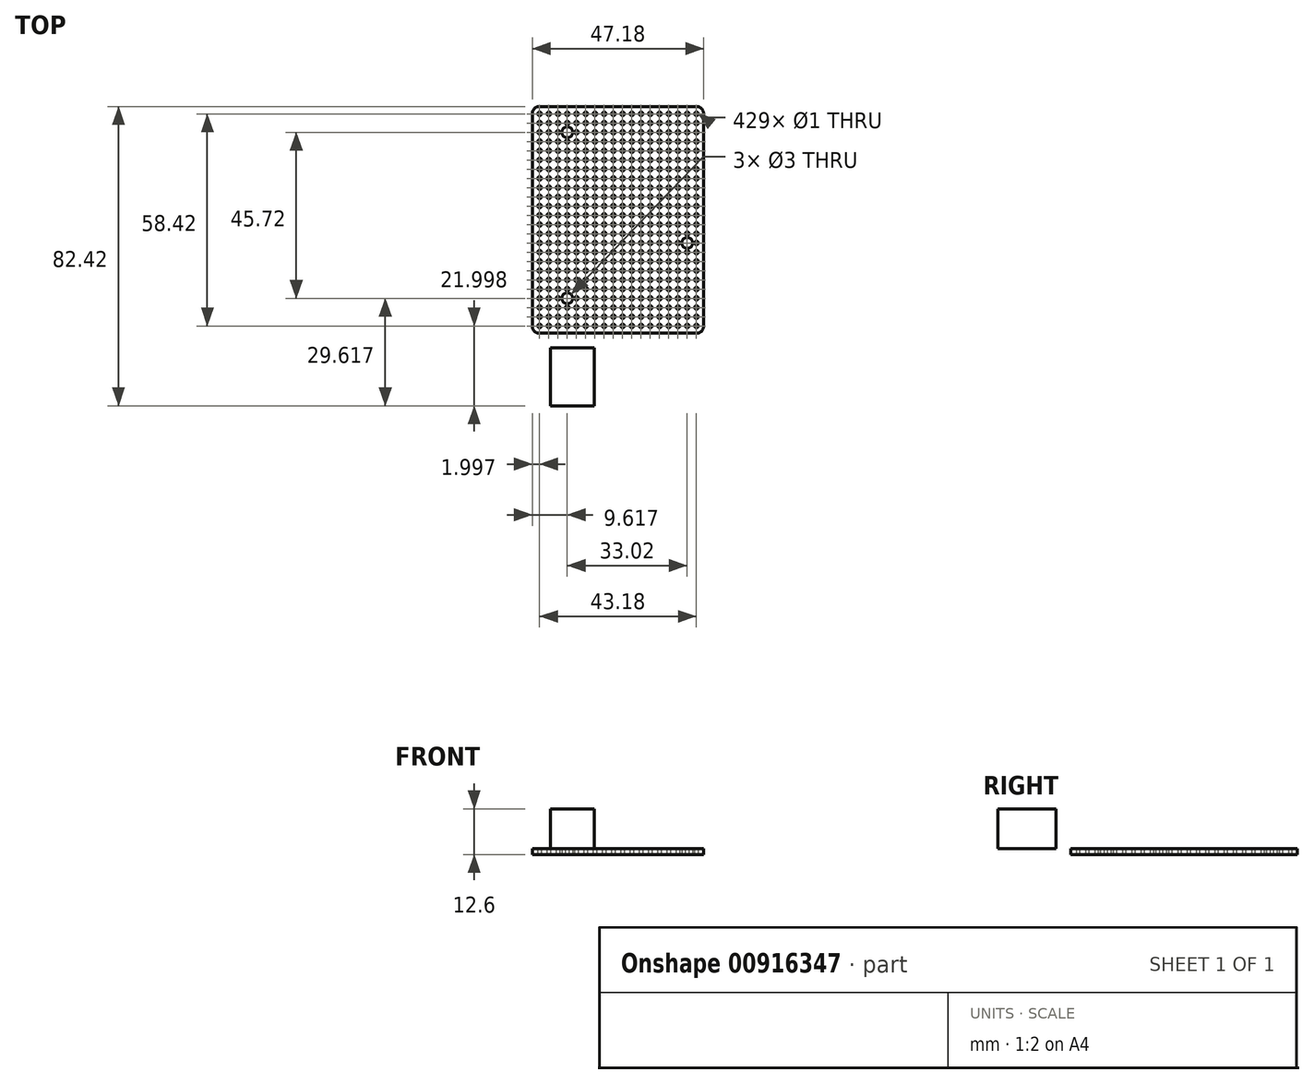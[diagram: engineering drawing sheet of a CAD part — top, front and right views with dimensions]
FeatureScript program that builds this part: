
annotation { "Feature Type Name" : "Feature", "Feature Type Description" : "" }
export const myFeature = defineFeature(function(context is Context, id is Id, definition is map)
    precondition{}
    {
        {
            var Q0;
            Q0=qCreatedBy(makeId("Top.planeOp"),FACE);
            var sketch = newSketch(context, id + "F0", { "sketchPlane" : qUnion([Q0])});
            skLineSegment(sketch, "E0.bottom", {"start": v(-24.1, 49.25) * mm, "end": v(23.09, 49.25) * mm});
            skLineSegment(sketch, "E0.top", {"start": v(-24.1, -13.17) * mm, "end": v(23.09, -13.17) * mm});
            skLineSegment(sketch, "E0.left", {"start": v(-24.1, 49.25) * mm, "end": v(-24.1, -13.17) * mm});
            skLineSegment(sketch, "E0.right", {"start": v(23.09, 49.25) * mm, "end": v(23.09, -13.17) * mm});
            skCircle(sketch, "E1", {"center": v(-22.1, 47.25) * mm, "radius": 0.5 * mm});
            skCircle(sketch, "E2.0.1.0", {"center": v(-22.1, 44.7) * mm, "radius": 0.5 * mm});
            skCircle(sketch, "E2.0.2.0", {"center": v(-22.1, 42.17) * mm, "radius": 0.5 * mm});
            skCircle(sketch, "E2.0.3.0", {"center": v(-22.1, 39.63) * mm, "radius": 0.5 * mm});
            skCircle(sketch, "E2.0.4.0", {"center": v(-22.1, 37.09) * mm, "radius": 0.5 * mm});
            skCircle(sketch, "E2.0.5.0", {"center": v(-22.1, 34.55) * mm, "radius": 0.5 * mm});
            skCircle(sketch, "E2.0.6.0", {"center": v(-22.1, 32) * mm, "radius": 0.5 * mm});
            skCircle(sketch, "E2.0.7.0", {"center": v(-22.1, 29.47) * mm, "radius": 0.5 * mm});
            skCircle(sketch, "E2.0.8.0", {"center": v(-22.1, 26.93) * mm, "radius": 0.5 * mm});
            skCircle(sketch, "E2.0.9.0", {"center": v(-22.1, 24.39) * mm, "radius": 0.5 * mm});
            skCircle(sketch, "E2.0.10.0", {"center": v(-22.1, 21.85) * mm, "radius": 0.5 * mm});
            skCircle(sketch, "E2.0.11.0", {"center": v(-22.1, 19.3) * mm, "radius": 0.5 * mm});
            skCircle(sketch, "E2.0.12.0", {"center": v(-22.1, 16.77) * mm, "radius": 0.5 * mm});
            skCircle(sketch, "E2.0.13.0", {"center": v(-22.1, 14.23) * mm, "radius": 0.5 * mm});
            skCircle(sketch, "E2.0.14.0", {"center": v(-22.1, 11.69) * mm, "radius": 0.5 * mm});
            skCircle(sketch, "E2.0.15.0", {"center": v(-22.1, 9.15) * mm, "radius": 0.5 * mm});
            skCircle(sketch, "E2.0.16.0", {"center": v(-22.1, 6.6) * mm, "radius": 0.5 * mm});
            skCircle(sketch, "E2.0.17.0", {"center": v(-22.1, 4.07) * mm, "radius": 0.5 * mm});
            skCircle(sketch, "E2.0.18.0", {"center": v(-22.1, 1.53) * mm, "radius": 0.5 * mm});
            skCircle(sketch, "E2.0.19.0", {"center": v(-22.1, -1.01) * mm, "radius": 0.5 * mm});
            skCircle(sketch, "E2.0.20.0", {"center": v(-22.1, -3.55) * mm, "radius": 0.5 * mm});
            skCircle(sketch, "E2.0.21.0", {"center": v(-22.1, -6.1) * mm, "radius": 0.5 * mm});
            skCircle(sketch, "E2.0.22.0", {"center": v(-22.1, -8.63) * mm, "radius": 0.5 * mm});
            skCircle(sketch, "E2.0.23.0", {"center": v(-22.1, -11.17) * mm, "radius": 0.5 * mm});
            skCircle(sketch, "E2.1.0.0", {"center": v(-19.55, 47.25) * mm, "radius": 0.5 * mm});
            skCircle(sketch, "E2.1.1.0", {"center": v(-19.55, 44.7) * mm, "radius": 0.5 * mm});
            skCircle(sketch, "E2.1.2.0", {"center": v(-19.55, 42.17) * mm, "radius": 0.5 * mm});
            skCircle(sketch, "E2.1.3.0", {"center": v(-19.55, 39.63) * mm, "radius": 0.5 * mm});
            skCircle(sketch, "E2.1.4.0", {"center": v(-19.55, 37.09) * mm, "radius": 0.5 * mm});
            skCircle(sketch, "E2.1.5.0", {"center": v(-19.55, 34.55) * mm, "radius": 0.5 * mm});
            skCircle(sketch, "E2.1.6.0", {"center": v(-19.55, 32) * mm, "radius": 0.5 * mm});
            skCircle(sketch, "E2.1.7.0", {"center": v(-19.55, 29.47) * mm, "radius": 0.5 * mm});
            skCircle(sketch, "E2.1.8.0", {"center": v(-19.55, 26.93) * mm, "radius": 0.5 * mm});
            skCircle(sketch, "E2.1.9.0", {"center": v(-19.55, 24.39) * mm, "radius": 0.5 * mm});
            skCircle(sketch, "E2.1.10.0", {"center": v(-19.55, 21.85) * mm, "radius": 0.5 * mm});
            skCircle(sketch, "E2.1.11.0", {"center": v(-19.55, 19.3) * mm, "radius": 0.5 * mm});
            skCircle(sketch, "E2.1.12.0", {"center": v(-19.55, 16.77) * mm, "radius": 0.5 * mm});
            skCircle(sketch, "E2.1.13.0", {"center": v(-19.55, 14.23) * mm, "radius": 0.5 * mm});
            skCircle(sketch, "E2.1.14.0", {"center": v(-19.55, 11.69) * mm, "radius": 0.5 * mm});
            skCircle(sketch, "E2.1.15.0", {"center": v(-19.55, 9.15) * mm, "radius": 0.5 * mm});
            skCircle(sketch, "E2.1.16.0", {"center": v(-19.55, 6.6) * mm, "radius": 0.5 * mm});
            skCircle(sketch, "E2.1.17.0", {"center": v(-19.55, 4.07) * mm, "radius": 0.5 * mm});
            skCircle(sketch, "E2.1.18.0", {"center": v(-19.55, 1.53) * mm, "radius": 0.5 * mm});
            skCircle(sketch, "E2.1.19.0", {"center": v(-19.55, -1.01) * mm, "radius": 0.5 * mm});
            skCircle(sketch, "E2.1.20.0", {"center": v(-19.55, -3.55) * mm, "radius": 0.5 * mm});
            skCircle(sketch, "E2.1.21.0", {"center": v(-19.55, -6.1) * mm, "radius": 0.5 * mm});
            skCircle(sketch, "E2.1.22.0", {"center": v(-19.55, -8.63) * mm, "radius": 0.5 * mm});
            skCircle(sketch, "E2.1.23.0", {"center": v(-19.55, -11.17) * mm, "radius": 0.5 * mm});
            skCircle(sketch, "E2.2.0.0", {"center": v(-17.01, 47.25) * mm, "radius": 0.5 * mm});
            skCircle(sketch, "E2.2.1.0", {"center": v(-17.01, 44.7) * mm, "radius": 0.5 * mm});
            skCircle(sketch, "E2.2.2.0", {"center": v(-17.01, 42.17) * mm, "radius": 0.5 * mm});
            skCircle(sketch, "E2.2.3.0", {"center": v(-17.01, 39.63) * mm, "radius": 0.5 * mm});
            skCircle(sketch, "E2.2.4.0", {"center": v(-17.01, 37.09) * mm, "radius": 0.5 * mm});
            skCircle(sketch, "E2.2.5.0", {"center": v(-17.01, 34.55) * mm, "radius": 0.5 * mm});
            skCircle(sketch, "E2.2.6.0", {"center": v(-17.01, 32) * mm, "radius": 0.5 * mm});
            skCircle(sketch, "E2.2.7.0", {"center": v(-17.01, 29.47) * mm, "radius": 0.5 * mm});
            skCircle(sketch, "E2.2.8.0", {"center": v(-17.01, 26.93) * mm, "radius": 0.5 * mm});
            skCircle(sketch, "E2.2.9.0", {"center": v(-17.01, 24.39) * mm, "radius": 0.5 * mm});
            skCircle(sketch, "E2.2.10.0", {"center": v(-17.01, 21.85) * mm, "radius": 0.5 * mm});
            skCircle(sketch, "E2.2.11.0", {"center": v(-17.01, 19.3) * mm, "radius": 0.5 * mm});
            skCircle(sketch, "E2.2.12.0", {"center": v(-17.01, 16.77) * mm, "radius": 0.5 * mm});
            skCircle(sketch, "E2.2.13.0", {"center": v(-17.01, 14.23) * mm, "radius": 0.5 * mm});
            skCircle(sketch, "E2.2.14.0", {"center": v(-17.01, 11.69) * mm, "radius": 0.5 * mm});
            skCircle(sketch, "E2.2.15.0", {"center": v(-17.01, 9.15) * mm, "radius": 0.5 * mm});
            skCircle(sketch, "E2.2.16.0", {"center": v(-17.01, 6.6) * mm, "radius": 0.5 * mm});
            skCircle(sketch, "E2.2.17.0", {"center": v(-17.01, 4.07) * mm, "radius": 0.5 * mm});
            skCircle(sketch, "E2.2.18.0", {"center": v(-17.01, 1.53) * mm, "radius": 0.5 * mm});
            skCircle(sketch, "E2.2.19.0", {"center": v(-17.01, -1.01) * mm, "radius": 0.5 * mm});
            skCircle(sketch, "E2.2.20.0", {"center": v(-17.01, -3.55) * mm, "radius": 0.5 * mm});
            skCircle(sketch, "E2.2.21.0", {"center": v(-17.01, -6.1) * mm, "radius": 0.5 * mm});
            skCircle(sketch, "E2.2.22.0", {"center": v(-17.01, -8.63) * mm, "radius": 0.5 * mm});
            skCircle(sketch, "E2.2.23.0", {"center": v(-17.01, -11.17) * mm, "radius": 0.5 * mm});
            skCircle(sketch, "E2.3.0.0", {"center": v(-14.47, 47.25) * mm, "radius": 0.5 * mm});
            skCircle(sketch, "E2.3.1.0", {"center": v(-14.47, 44.7) * mm, "radius": 0.5 * mm});
            skCircle(sketch, "E2.3.2.0", {"center": v(-14.47, 42.17) * mm, "radius": 0.5 * mm});
            skCircle(sketch, "E2.3.3.0", {"center": v(-14.47, 39.63) * mm, "radius": 0.5 * mm});
            skCircle(sketch, "E2.3.4.0", {"center": v(-14.47, 37.09) * mm, "radius": 0.5 * mm});
            skCircle(sketch, "E2.3.5.0", {"center": v(-14.47, 34.55) * mm, "radius": 0.5 * mm});
            skCircle(sketch, "E2.3.6.0", {"center": v(-14.47, 32) * mm, "radius": 0.5 * mm});
            skCircle(sketch, "E2.3.7.0", {"center": v(-14.47, 29.47) * mm, "radius": 0.5 * mm});
            skCircle(sketch, "E2.3.8.0", {"center": v(-14.47, 26.93) * mm, "radius": 0.5 * mm});
            skCircle(sketch, "E2.3.9.0", {"center": v(-14.47, 24.39) * mm, "radius": 0.5 * mm});
            skCircle(sketch, "E2.3.10.0", {"center": v(-14.47, 21.85) * mm, "radius": 0.5 * mm});
            skCircle(sketch, "E2.3.11.0", {"center": v(-14.47, 19.3) * mm, "radius": 0.5 * mm});
            skCircle(sketch, "E2.3.12.0", {"center": v(-14.47, 16.77) * mm, "radius": 0.5 * mm});
            skCircle(sketch, "E2.3.13.0", {"center": v(-14.47, 14.23) * mm, "radius": 0.5 * mm});
            skCircle(sketch, "E2.3.14.0", {"center": v(-14.47, 11.69) * mm, "radius": 0.5 * mm});
            skCircle(sketch, "E2.3.15.0", {"center": v(-14.47, 9.15) * mm, "radius": 0.5 * mm});
            skCircle(sketch, "E2.3.16.0", {"center": v(-14.47, 6.6) * mm, "radius": 0.5 * mm});
            skCircle(sketch, "E2.3.17.0", {"center": v(-14.47, 4.07) * mm, "radius": 0.5 * mm});
            skCircle(sketch, "E2.3.18.0", {"center": v(-14.47, 1.53) * mm, "radius": 0.5 * mm});
            skCircle(sketch, "E2.3.19.0", {"center": v(-14.47, -1.01) * mm, "radius": 0.5 * mm});
            skCircle(sketch, "E2.3.20.0", {"center": v(-14.47, -3.55) * mm, "radius": 0.5 * mm});
            skCircle(sketch, "E2.3.21.0", {"center": v(-14.47, -6.1) * mm, "radius": 0.5 * mm});
            skCircle(sketch, "E2.3.22.0", {"center": v(-14.47, -8.63) * mm, "radius": 0.5 * mm});
            skCircle(sketch, "E2.3.23.0", {"center": v(-14.47, -11.17) * mm, "radius": 0.5 * mm});
            skCircle(sketch, "E2.4.0.0", {"center": v(-11.93, 47.25) * mm, "radius": 0.5 * mm});
            skCircle(sketch, "E2.4.1.0", {"center": v(-11.93, 44.7) * mm, "radius": 0.5 * mm});
            skCircle(sketch, "E2.4.2.0", {"center": v(-11.93, 42.17) * mm, "radius": 0.5 * mm});
            skCircle(sketch, "E2.4.3.0", {"center": v(-11.93, 39.63) * mm, "radius": 0.5 * mm});
            skCircle(sketch, "E2.4.4.0", {"center": v(-11.93, 37.09) * mm, "radius": 0.5 * mm});
            skCircle(sketch, "E2.4.5.0", {"center": v(-11.93, 34.55) * mm, "radius": 0.5 * mm});
            skCircle(sketch, "E2.4.6.0", {"center": v(-11.93, 32) * mm, "radius": 0.5 * mm});
            skCircle(sketch, "E2.4.7.0", {"center": v(-11.93, 29.47) * mm, "radius": 0.5 * mm});
            skCircle(sketch, "E2.4.8.0", {"center": v(-11.93, 26.93) * mm, "radius": 0.5 * mm});
            skCircle(sketch, "E2.4.9.0", {"center": v(-11.93, 24.39) * mm, "radius": 0.5 * mm});
            skCircle(sketch, "E2.4.10.0", {"center": v(-11.93, 21.85) * mm, "radius": 0.5 * mm});
            skCircle(sketch, "E2.4.11.0", {"center": v(-11.93, 19.3) * mm, "radius": 0.5 * mm});
            skCircle(sketch, "E2.4.12.0", {"center": v(-11.93, 16.77) * mm, "radius": 0.5 * mm});
            skCircle(sketch, "E2.4.13.0", {"center": v(-11.93, 14.23) * mm, "radius": 0.5 * mm});
            skCircle(sketch, "E2.4.14.0", {"center": v(-11.93, 11.69) * mm, "radius": 0.5 * mm});
            skCircle(sketch, "E2.4.15.0", {"center": v(-11.93, 9.15) * mm, "radius": 0.5 * mm});
            skCircle(sketch, "E2.4.16.0", {"center": v(-11.93, 6.6) * mm, "radius": 0.5 * mm});
            skCircle(sketch, "E2.4.17.0", {"center": v(-11.93, 4.07) * mm, "radius": 0.5 * mm});
            skCircle(sketch, "E2.4.18.0", {"center": v(-11.93, 1.53) * mm, "radius": 0.5 * mm});
            skCircle(sketch, "E2.4.19.0", {"center": v(-11.93, -1.01) * mm, "radius": 0.5 * mm});
            skCircle(sketch, "E2.4.20.0", {"center": v(-11.93, -3.55) * mm, "radius": 0.5 * mm});
            skCircle(sketch, "E2.4.21.0", {"center": v(-11.93, -6.1) * mm, "radius": 0.5 * mm});
            skCircle(sketch, "E2.4.22.0", {"center": v(-11.93, -8.63) * mm, "radius": 0.5 * mm});
            skCircle(sketch, "E2.4.23.0", {"center": v(-11.93, -11.17) * mm, "radius": 0.5 * mm});
            skCircle(sketch, "E2.5.0.0", {"center": v(-9.4, 47.25) * mm, "radius": 0.5 * mm});
            skCircle(sketch, "E2.5.1.0", {"center": v(-9.4, 44.7) * mm, "radius": 0.5 * mm});
            skCircle(sketch, "E2.5.2.0", {"center": v(-9.4, 42.17) * mm, "radius": 0.5 * mm});
            skCircle(sketch, "E2.5.3.0", {"center": v(-9.4, 39.63) * mm, "radius": 0.5 * mm});
            skCircle(sketch, "E2.5.4.0", {"center": v(-9.4, 37.09) * mm, "radius": 0.5 * mm});
            skCircle(sketch, "E2.5.5.0", {"center": v(-9.4, 34.55) * mm, "radius": 0.5 * mm});
            skCircle(sketch, "E2.5.6.0", {"center": v(-9.4, 32) * mm, "radius": 0.5 * mm});
            skCircle(sketch, "E2.5.7.0", {"center": v(-9.4, 29.47) * mm, "radius": 0.5 * mm});
            skCircle(sketch, "E2.5.8.0", {"center": v(-9.4, 26.93) * mm, "radius": 0.5 * mm});
            skCircle(sketch, "E2.5.9.0", {"center": v(-9.4, 24.39) * mm, "radius": 0.5 * mm});
            skCircle(sketch, "E2.5.10.0", {"center": v(-9.4, 21.85) * mm, "radius": 0.5 * mm});
            skCircle(sketch, "E2.5.11.0", {"center": v(-9.4, 19.3) * mm, "radius": 0.5 * mm});
            skCircle(sketch, "E2.5.12.0", {"center": v(-9.4, 16.77) * mm, "radius": 0.5 * mm});
            skCircle(sketch, "E2.5.13.0", {"center": v(-9.4, 14.23) * mm, "radius": 0.5 * mm});
            skCircle(sketch, "E2.5.14.0", {"center": v(-9.4, 11.69) * mm, "radius": 0.5 * mm});
            skCircle(sketch, "E2.5.15.0", {"center": v(-9.4, 9.15) * mm, "radius": 0.5 * mm});
            skCircle(sketch, "E2.5.16.0", {"center": v(-9.4, 6.6) * mm, "radius": 0.5 * mm});
            skCircle(sketch, "E2.5.17.0", {"center": v(-9.4, 4.07) * mm, "radius": 0.5 * mm});
            skCircle(sketch, "E2.5.18.0", {"center": v(-9.4, 1.53) * mm, "radius": 0.5 * mm});
            skCircle(sketch, "E2.5.19.0", {"center": v(-9.4, -1.01) * mm, "radius": 0.5 * mm});
            skCircle(sketch, "E2.5.20.0", {"center": v(-9.4, -3.55) * mm, "radius": 0.5 * mm});
            skCircle(sketch, "E2.5.21.0", {"center": v(-9.4, -6.1) * mm, "radius": 0.5 * mm});
            skCircle(sketch, "E2.5.22.0", {"center": v(-9.4, -8.63) * mm, "radius": 0.5 * mm});
            skCircle(sketch, "E2.5.23.0", {"center": v(-9.4, -11.17) * mm, "radius": 0.5 * mm});
            skCircle(sketch, "E2.6.0.0", {"center": v(-6.85, 47.25) * mm, "radius": 0.5 * mm});
            skCircle(sketch, "E2.6.1.0", {"center": v(-6.85, 44.7) * mm, "radius": 0.5 * mm});
            skCircle(sketch, "E2.6.2.0", {"center": v(-6.85, 42.17) * mm, "radius": 0.5 * mm});
            skCircle(sketch, "E2.6.3.0", {"center": v(-6.85, 39.63) * mm, "radius": 0.5 * mm});
            skCircle(sketch, "E2.6.4.0", {"center": v(-6.85, 37.09) * mm, "radius": 0.5 * mm});
            skCircle(sketch, "E2.6.5.0", {"center": v(-6.85, 34.55) * mm, "radius": 0.5 * mm});
            skCircle(sketch, "E2.6.6.0", {"center": v(-6.85, 32) * mm, "radius": 0.5 * mm});
            skCircle(sketch, "E2.6.7.0", {"center": v(-6.85, 29.47) * mm, "radius": 0.5 * mm});
            skCircle(sketch, "E2.6.8.0", {"center": v(-6.85, 26.93) * mm, "radius": 0.5 * mm});
            skCircle(sketch, "E2.6.9.0", {"center": v(-6.85, 24.39) * mm, "radius": 0.5 * mm});
            skCircle(sketch, "E2.6.10.0", {"center": v(-6.85, 21.85) * mm, "radius": 0.5 * mm});
            skCircle(sketch, "E2.6.11.0", {"center": v(-6.85, 19.3) * mm, "radius": 0.5 * mm});
            skCircle(sketch, "E2.6.12.0", {"center": v(-6.85, 16.77) * mm, "radius": 0.5 * mm});
            skCircle(sketch, "E2.6.13.0", {"center": v(-6.85, 14.23) * mm, "radius": 0.5 * mm});
            skCircle(sketch, "E2.6.14.0", {"center": v(-6.85, 11.69) * mm, "radius": 0.5 * mm});
            skCircle(sketch, "E2.6.15.0", {"center": v(-6.85, 9.15) * mm, "radius": 0.5 * mm});
            skCircle(sketch, "E2.6.16.0", {"center": v(-6.85, 6.6) * mm, "radius": 0.5 * mm});
            skCircle(sketch, "E2.6.17.0", {"center": v(-6.85, 4.07) * mm, "radius": 0.5 * mm});
            skCircle(sketch, "E2.6.18.0", {"center": v(-6.85, 1.53) * mm, "radius": 0.5 * mm});
            skCircle(sketch, "E2.6.19.0", {"center": v(-6.85, -1.01) * mm, "radius": 0.5 * mm});
            skCircle(sketch, "E2.6.20.0", {"center": v(-6.85, -3.55) * mm, "radius": 0.5 * mm});
            skCircle(sketch, "E2.6.21.0", {"center": v(-6.85, -6.1) * mm, "radius": 0.5 * mm});
            skCircle(sketch, "E2.6.22.0", {"center": v(-6.85, -8.63) * mm, "radius": 0.5 * mm});
            skCircle(sketch, "E2.6.23.0", {"center": v(-6.85, -11.17) * mm, "radius": 0.5 * mm});
            skCircle(sketch, "E2.7.0.0", {"center": v(-4.31, 47.25) * mm, "radius": 0.5 * mm});
            skCircle(sketch, "E2.7.1.0", {"center": v(-4.31, 44.7) * mm, "radius": 0.5 * mm});
            skCircle(sketch, "E2.7.2.0", {"center": v(-4.31, 42.17) * mm, "radius": 0.5 * mm});
            skCircle(sketch, "E2.7.3.0", {"center": v(-4.31, 39.63) * mm, "radius": 0.5 * mm});
            skCircle(sketch, "E2.7.4.0", {"center": v(-4.31, 37.09) * mm, "radius": 0.5 * mm});
            skCircle(sketch, "E2.7.5.0", {"center": v(-4.31, 34.55) * mm, "radius": 0.5 * mm});
            skCircle(sketch, "E2.7.6.0", {"center": v(-4.31, 32) * mm, "radius": 0.5 * mm});
            skCircle(sketch, "E2.7.7.0", {"center": v(-4.31, 29.47) * mm, "radius": 0.5 * mm});
            skCircle(sketch, "E2.7.8.0", {"center": v(-4.31, 26.93) * mm, "radius": 0.5 * mm});
            skCircle(sketch, "E2.7.9.0", {"center": v(-4.31, 24.39) * mm, "radius": 0.5 * mm});
            skCircle(sketch, "E2.7.10.0", {"center": v(-4.31, 21.85) * mm, "radius": 0.5 * mm});
            skCircle(sketch, "E2.7.11.0", {"center": v(-4.31, 19.3) * mm, "radius": 0.5 * mm});
            skCircle(sketch, "E2.7.12.0", {"center": v(-4.31, 16.77) * mm, "radius": 0.5 * mm});
            skCircle(sketch, "E2.7.13.0", {"center": v(-4.31, 14.23) * mm, "radius": 0.5 * mm});
            skCircle(sketch, "E2.7.14.0", {"center": v(-4.31, 11.69) * mm, "radius": 0.5 * mm});
            skCircle(sketch, "E2.7.15.0", {"center": v(-4.31, 9.15) * mm, "radius": 0.5 * mm});
            skCircle(sketch, "E2.7.16.0", {"center": v(-4.31, 6.6) * mm, "radius": 0.5 * mm});
            skCircle(sketch, "E2.7.17.0", {"center": v(-4.31, 4.07) * mm, "radius": 0.5 * mm});
            skCircle(sketch, "E2.7.18.0", {"center": v(-4.31, 1.53) * mm, "radius": 0.5 * mm});
            skCircle(sketch, "E2.7.19.0", {"center": v(-4.31, -1.01) * mm, "radius": 0.5 * mm});
            skCircle(sketch, "E2.7.20.0", {"center": v(-4.31, -3.55) * mm, "radius": 0.5 * mm});
            skCircle(sketch, "E2.7.21.0", {"center": v(-4.31, -6.1) * mm, "radius": 0.5 * mm});
            skCircle(sketch, "E2.7.22.0", {"center": v(-4.31, -8.63) * mm, "radius": 0.5 * mm});
            skCircle(sketch, "E2.7.23.0", {"center": v(-4.31, -11.17) * mm, "radius": 0.5 * mm});
            skCircle(sketch, "E2.8.0.0", {"center": v(-1.77, 47.25) * mm, "radius": 0.5 * mm});
            skCircle(sketch, "E2.8.1.0", {"center": v(-1.77, 44.7) * mm, "radius": 0.5 * mm});
            skCircle(sketch, "E2.8.2.0", {"center": v(-1.77, 42.17) * mm, "radius": 0.5 * mm});
            skCircle(sketch, "E2.8.3.0", {"center": v(-1.77, 39.63) * mm, "radius": 0.5 * mm});
            skCircle(sketch, "E2.8.4.0", {"center": v(-1.77, 37.09) * mm, "radius": 0.5 * mm});
            skCircle(sketch, "E2.8.5.0", {"center": v(-1.77, 34.55) * mm, "radius": 0.5 * mm});
            skCircle(sketch, "E2.8.6.0", {"center": v(-1.77, 32) * mm, "radius": 0.5 * mm});
            skCircle(sketch, "E2.8.7.0", {"center": v(-1.77, 29.47) * mm, "radius": 0.5 * mm});
            skCircle(sketch, "E2.8.8.0", {"center": v(-1.77, 26.93) * mm, "radius": 0.5 * mm});
            skCircle(sketch, "E2.8.9.0", {"center": v(-1.77, 24.39) * mm, "radius": 0.5 * mm});
            skCircle(sketch, "E2.8.10.0", {"center": v(-1.77, 21.85) * mm, "radius": 0.5 * mm});
            skCircle(sketch, "E2.8.11.0", {"center": v(-1.77, 19.3) * mm, "radius": 0.5 * mm});
            skCircle(sketch, "E2.8.12.0", {"center": v(-1.77, 16.77) * mm, "radius": 0.5 * mm});
            skCircle(sketch, "E2.8.13.0", {"center": v(-1.77, 14.23) * mm, "radius": 0.5 * mm});
            skCircle(sketch, "E2.8.14.0", {"center": v(-1.77, 11.69) * mm, "radius": 0.5 * mm});
            skCircle(sketch, "E2.8.15.0", {"center": v(-1.77, 9.15) * mm, "radius": 0.5 * mm});
            skCircle(sketch, "E2.8.16.0", {"center": v(-1.77, 6.6) * mm, "radius": 0.5 * mm});
            skCircle(sketch, "E2.8.17.0", {"center": v(-1.77, 4.07) * mm, "radius": 0.5 * mm});
            skCircle(sketch, "E2.8.18.0", {"center": v(-1.77, 1.53) * mm, "radius": 0.5 * mm});
            skCircle(sketch, "E2.8.19.0", {"center": v(-1.77, -1.01) * mm, "radius": 0.5 * mm});
            skCircle(sketch, "E2.8.20.0", {"center": v(-1.77, -3.55) * mm, "radius": 0.5 * mm});
            skCircle(sketch, "E2.8.21.0", {"center": v(-1.77, -6.1) * mm, "radius": 0.5 * mm});
            skCircle(sketch, "E2.8.22.0", {"center": v(-1.77, -8.63) * mm, "radius": 0.5 * mm});
            skCircle(sketch, "E2.8.23.0", {"center": v(-1.77, -11.17) * mm, "radius": 0.5 * mm});
            skCircle(sketch, "E2.9.0.0", {"center": v(0.77, 47.25) * mm, "radius": 0.5 * mm});
            skCircle(sketch, "E2.9.1.0", {"center": v(0.77, 44.7) * mm, "radius": 0.5 * mm});
            skCircle(sketch, "E2.9.2.0", {"center": v(0.77, 42.17) * mm, "radius": 0.5 * mm});
            skCircle(sketch, "E2.9.3.0", {"center": v(0.77, 39.63) * mm, "radius": 0.5 * mm});
            skCircle(sketch, "E2.9.4.0", {"center": v(0.77, 37.09) * mm, "radius": 0.5 * mm});
            skCircle(sketch, "E2.9.5.0", {"center": v(0.77, 34.55) * mm, "radius": 0.5 * mm});
            skCircle(sketch, "E2.9.6.0", {"center": v(0.77, 32) * mm, "radius": 0.5 * mm});
            skCircle(sketch, "E2.9.7.0", {"center": v(0.77, 29.47) * mm, "radius": 0.5 * mm});
            skCircle(sketch, "E2.9.8.0", {"center": v(0.77, 26.93) * mm, "radius": 0.5 * mm});
            skCircle(sketch, "E2.9.9.0", {"center": v(0.77, 24.39) * mm, "radius": 0.5 * mm});
            skCircle(sketch, "E2.9.10.0", {"center": v(0.77, 21.85) * mm, "radius": 0.5 * mm});
            skCircle(sketch, "E2.9.11.0", {"center": v(0.77, 19.3) * mm, "radius": 0.5 * mm});
            skCircle(sketch, "E2.9.12.0", {"center": v(0.77, 16.77) * mm, "radius": 0.5 * mm});
            skCircle(sketch, "E2.9.13.0", {"center": v(0.77, 14.23) * mm, "radius": 0.5 * mm});
            skCircle(sketch, "E2.9.14.0", {"center": v(0.77, 11.69) * mm, "radius": 0.5 * mm});
            skCircle(sketch, "E2.9.15.0", {"center": v(0.77, 9.15) * mm, "radius": 0.5 * mm});
            skCircle(sketch, "E2.9.16.0", {"center": v(0.77, 6.6) * mm, "radius": 0.5 * mm});
            skCircle(sketch, "E2.9.17.0", {"center": v(0.77, 4.07) * mm, "radius": 0.5 * mm});
            skCircle(sketch, "E2.9.18.0", {"center": v(0.77, 1.53) * mm, "radius": 0.5 * mm});
            skCircle(sketch, "E2.9.19.0", {"center": v(0.77, -1.01) * mm, "radius": 0.5 * mm});
            skCircle(sketch, "E2.9.20.0", {"center": v(0.77, -3.55) * mm, "radius": 0.5 * mm});
            skCircle(sketch, "E2.9.21.0", {"center": v(0.77, -6.1) * mm, "radius": 0.5 * mm});
            skCircle(sketch, "E2.9.22.0", {"center": v(0.77, -8.63) * mm, "radius": 0.5 * mm});
            skCircle(sketch, "E2.9.23.0", {"center": v(0.77, -11.17) * mm, "radius": 0.5 * mm});
            skCircle(sketch, "E2.10.0.0", {"center": v(3.3, 47.25) * mm, "radius": 0.5 * mm});
            skCircle(sketch, "E2.10.1.0", {"center": v(3.3, 44.7) * mm, "radius": 0.5 * mm});
            skCircle(sketch, "E2.10.2.0", {"center": v(3.3, 42.17) * mm, "radius": 0.5 * mm});
            skCircle(sketch, "E2.10.3.0", {"center": v(3.3, 39.63) * mm, "radius": 0.5 * mm});
            skCircle(sketch, "E2.10.4.0", {"center": v(3.3, 37.09) * mm, "radius": 0.5 * mm});
            skCircle(sketch, "E2.10.5.0", {"center": v(3.3, 34.55) * mm, "radius": 0.5 * mm});
            skCircle(sketch, "E2.10.6.0", {"center": v(3.3, 32) * mm, "radius": 0.5 * mm});
            skCircle(sketch, "E2.10.7.0", {"center": v(3.3, 29.47) * mm, "radius": 0.5 * mm});
            skCircle(sketch, "E2.10.8.0", {"center": v(3.3, 26.93) * mm, "radius": 0.5 * mm});
            skCircle(sketch, "E2.10.9.0", {"center": v(3.3, 24.39) * mm, "radius": 0.5 * mm});
            skCircle(sketch, "E2.10.10.0", {"center": v(3.3, 21.85) * mm, "radius": 0.5 * mm});
            skCircle(sketch, "E2.10.11.0", {"center": v(3.3, 19.3) * mm, "radius": 0.5 * mm});
            skCircle(sketch, "E2.10.12.0", {"center": v(3.3, 16.77) * mm, "radius": 0.5 * mm});
            skCircle(sketch, "E2.10.13.0", {"center": v(3.3, 14.23) * mm, "radius": 0.5 * mm});
            skCircle(sketch, "E2.10.14.0", {"center": v(3.3, 11.69) * mm, "radius": 0.5 * mm});
            skCircle(sketch, "E2.10.15.0", {"center": v(3.3, 9.15) * mm, "radius": 0.5 * mm});
            skCircle(sketch, "E2.10.16.0", {"center": v(3.3, 6.6) * mm, "radius": 0.5 * mm});
            skCircle(sketch, "E2.10.17.0", {"center": v(3.3, 4.07) * mm, "radius": 0.5 * mm});
            skCircle(sketch, "E2.10.18.0", {"center": v(3.3, 1.53) * mm, "radius": 0.5 * mm});
            skCircle(sketch, "E2.10.19.0", {"center": v(3.3, -1.01) * mm, "radius": 0.5 * mm});
            skCircle(sketch, "E2.10.20.0", {"center": v(3.3, -3.55) * mm, "radius": 0.5 * mm});
            skCircle(sketch, "E2.10.21.0", {"center": v(3.3, -6.1) * mm, "radius": 0.5 * mm});
            skCircle(sketch, "E2.10.22.0", {"center": v(3.3, -8.63) * mm, "radius": 0.5 * mm});
            skCircle(sketch, "E2.10.23.0", {"center": v(3.3, -11.17) * mm, "radius": 0.5 * mm});
            skCircle(sketch, "E2.11.0.0", {"center": v(5.85, 47.25) * mm, "radius": 0.5 * mm});
            skCircle(sketch, "E2.11.1.0", {"center": v(5.85, 44.7) * mm, "radius": 0.5 * mm});
            skCircle(sketch, "E2.11.2.0", {"center": v(5.85, 42.17) * mm, "radius": 0.5 * mm});
            skCircle(sketch, "E2.11.3.0", {"center": v(5.85, 39.63) * mm, "radius": 0.5 * mm});
            skCircle(sketch, "E2.11.4.0", {"center": v(5.85, 37.09) * mm, "radius": 0.5 * mm});
            skCircle(sketch, "E2.11.5.0", {"center": v(5.85, 34.55) * mm, "radius": 0.5 * mm});
            skCircle(sketch, "E2.11.6.0", {"center": v(5.85, 32) * mm, "radius": 0.5 * mm});
            skCircle(sketch, "E2.11.7.0", {"center": v(5.85, 29.47) * mm, "radius": 0.5 * mm});
            skCircle(sketch, "E2.11.8.0", {"center": v(5.85, 26.93) * mm, "radius": 0.5 * mm});
            skCircle(sketch, "E2.11.9.0", {"center": v(5.85, 24.39) * mm, "radius": 0.5 * mm});
            skCircle(sketch, "E2.11.10.0", {"center": v(5.85, 21.85) * mm, "radius": 0.5 * mm});
            skCircle(sketch, "E2.11.11.0", {"center": v(5.85, 19.3) * mm, "radius": 0.5 * mm});
            skCircle(sketch, "E2.11.12.0", {"center": v(5.85, 16.77) * mm, "radius": 0.5 * mm});
            skCircle(sketch, "E2.11.13.0", {"center": v(5.85, 14.23) * mm, "radius": 0.5 * mm});
            skCircle(sketch, "E2.11.14.0", {"center": v(5.85, 11.69) * mm, "radius": 0.5 * mm});
            skCircle(sketch, "E2.11.15.0", {"center": v(5.85, 9.15) * mm, "radius": 0.5 * mm});
            skCircle(sketch, "E2.11.16.0", {"center": v(5.85, 6.6) * mm, "radius": 0.5 * mm});
            skCircle(sketch, "E2.11.17.0", {"center": v(5.85, 4.07) * mm, "radius": 0.5 * mm});
            skCircle(sketch, "E2.11.18.0", {"center": v(5.85, 1.53) * mm, "radius": 0.5 * mm});
            skCircle(sketch, "E2.11.19.0", {"center": v(5.85, -1.01) * mm, "radius": 0.5 * mm});
            skCircle(sketch, "E2.11.20.0", {"center": v(5.85, -3.55) * mm, "radius": 0.5 * mm});
            skCircle(sketch, "E2.11.21.0", {"center": v(5.85, -6.1) * mm, "radius": 0.5 * mm});
            skCircle(sketch, "E2.11.22.0", {"center": v(5.85, -8.63) * mm, "radius": 0.5 * mm});
            skCircle(sketch, "E2.11.23.0", {"center": v(5.85, -11.17) * mm, "radius": 0.5 * mm});
            skCircle(sketch, "E2.12.0.0", {"center": v(8.39, 47.25) * mm, "radius": 0.5 * mm});
            skCircle(sketch, "E2.12.1.0", {"center": v(8.39, 44.7) * mm, "radius": 0.5 * mm});
            skCircle(sketch, "E2.12.2.0", {"center": v(8.39, 42.17) * mm, "radius": 0.5 * mm});
            skCircle(sketch, "E2.12.3.0", {"center": v(8.39, 39.63) * mm, "radius": 0.5 * mm});
            skCircle(sketch, "E2.12.4.0", {"center": v(8.39, 37.09) * mm, "radius": 0.5 * mm});
            skCircle(sketch, "E2.12.5.0", {"center": v(8.39, 34.55) * mm, "radius": 0.5 * mm});
            skCircle(sketch, "E2.12.6.0", {"center": v(8.39, 32) * mm, "radius": 0.5 * mm});
            skCircle(sketch, "E2.12.7.0", {"center": v(8.39, 29.47) * mm, "radius": 0.5 * mm});
            skCircle(sketch, "E2.12.8.0", {"center": v(8.39, 26.93) * mm, "radius": 0.5 * mm});
            skCircle(sketch, "E2.12.9.0", {"center": v(8.39, 24.39) * mm, "radius": 0.5 * mm});
            skCircle(sketch, "E2.12.10.0", {"center": v(8.39, 21.85) * mm, "radius": 0.5 * mm});
            skCircle(sketch, "E2.12.11.0", {"center": v(8.39, 19.3) * mm, "radius": 0.5 * mm});
            skCircle(sketch, "E2.12.12.0", {"center": v(8.39, 16.77) * mm, "radius": 0.5 * mm});
            skCircle(sketch, "E2.12.13.0", {"center": v(8.39, 14.23) * mm, "radius": 0.5 * mm});
            skCircle(sketch, "E2.12.14.0", {"center": v(8.39, 11.69) * mm, "radius": 0.5 * mm});
            skCircle(sketch, "E2.12.15.0", {"center": v(8.39, 9.15) * mm, "radius": 0.5 * mm});
            skCircle(sketch, "E2.12.16.0", {"center": v(8.39, 6.6) * mm, "radius": 0.5 * mm});
            skCircle(sketch, "E2.12.17.0", {"center": v(8.39, 4.07) * mm, "radius": 0.5 * mm});
            skCircle(sketch, "E2.12.18.0", {"center": v(8.39, 1.53) * mm, "radius": 0.5 * mm});
            skCircle(sketch, "E2.12.19.0", {"center": v(8.39, -1.01) * mm, "radius": 0.5 * mm});
            skCircle(sketch, "E2.12.20.0", {"center": v(8.39, -3.55) * mm, "radius": 0.5 * mm});
            skCircle(sketch, "E2.12.21.0", {"center": v(8.39, -6.1) * mm, "radius": 0.5 * mm});
            skCircle(sketch, "E2.12.22.0", {"center": v(8.39, -8.63) * mm, "radius": 0.5 * mm});
            skCircle(sketch, "E2.12.23.0", {"center": v(8.39, -11.17) * mm, "radius": 0.5 * mm});
            skCircle(sketch, "E2.13.0.0", {"center": v(10.93, 47.25) * mm, "radius": 0.5 * mm});
            skCircle(sketch, "E2.13.1.0", {"center": v(10.93, 44.7) * mm, "radius": 0.5 * mm});
            skCircle(sketch, "E2.13.2.0", {"center": v(10.93, 42.17) * mm, "radius": 0.5 * mm});
            skCircle(sketch, "E2.13.3.0", {"center": v(10.93, 39.63) * mm, "radius": 0.5 * mm});
            skCircle(sketch, "E2.13.4.0", {"center": v(10.93, 37.09) * mm, "radius": 0.5 * mm});
            skCircle(sketch, "E2.13.5.0", {"center": v(10.93, 34.55) * mm, "radius": 0.5 * mm});
            skCircle(sketch, "E2.13.6.0", {"center": v(10.93, 32) * mm, "radius": 0.5 * mm});
            skCircle(sketch, "E2.13.7.0", {"center": v(10.93, 29.47) * mm, "radius": 0.5 * mm});
            skCircle(sketch, "E2.13.8.0", {"center": v(10.93, 26.93) * mm, "radius": 0.5 * mm});
            skCircle(sketch, "E2.13.9.0", {"center": v(10.93, 24.39) * mm, "radius": 0.5 * mm});
            skCircle(sketch, "E2.13.10.0", {"center": v(10.93, 21.85) * mm, "radius": 0.5 * mm});
            skCircle(sketch, "E2.13.11.0", {"center": v(10.93, 19.3) * mm, "radius": 0.5 * mm});
            skCircle(sketch, "E2.13.12.0", {"center": v(10.93, 16.77) * mm, "radius": 0.5 * mm});
            skCircle(sketch, "E2.13.13.0", {"center": v(10.93, 14.23) * mm, "radius": 0.5 * mm});
            skCircle(sketch, "E2.13.14.0", {"center": v(10.93, 11.69) * mm, "radius": 0.5 * mm});
            skCircle(sketch, "E2.13.15.0", {"center": v(10.93, 9.15) * mm, "radius": 0.5 * mm});
            skCircle(sketch, "E2.13.16.0", {"center": v(10.93, 6.6) * mm, "radius": 0.5 * mm});
            skCircle(sketch, "E2.13.17.0", {"center": v(10.93, 4.07) * mm, "radius": 0.5 * mm});
            skCircle(sketch, "E2.13.18.0", {"center": v(10.93, 1.53) * mm, "radius": 0.5 * mm});
            skCircle(sketch, "E2.13.19.0", {"center": v(10.93, -1.01) * mm, "radius": 0.5 * mm});
            skCircle(sketch, "E2.13.20.0", {"center": v(10.93, -3.55) * mm, "radius": 0.5 * mm});
            skCircle(sketch, "E2.13.21.0", {"center": v(10.93, -6.1) * mm, "radius": 0.5 * mm});
            skCircle(sketch, "E2.13.22.0", {"center": v(10.93, -8.63) * mm, "radius": 0.5 * mm});
            skCircle(sketch, "E2.13.23.0", {"center": v(10.93, -11.17) * mm, "radius": 0.5 * mm});
            skCircle(sketch, "E2.14.0.0", {"center": v(13.47, 47.25) * mm, "radius": 0.5 * mm});
            skCircle(sketch, "E2.14.1.0", {"center": v(13.47, 44.7) * mm, "radius": 0.5 * mm});
            skCircle(sketch, "E2.14.2.0", {"center": v(13.47, 42.17) * mm, "radius": 0.5 * mm});
            skCircle(sketch, "E2.14.3.0", {"center": v(13.47, 39.63) * mm, "radius": 0.5 * mm});
            skCircle(sketch, "E2.14.4.0", {"center": v(13.47, 37.09) * mm, "radius": 0.5 * mm});
            skCircle(sketch, "E2.14.5.0", {"center": v(13.47, 34.55) * mm, "radius": 0.5 * mm});
            skCircle(sketch, "E2.14.6.0", {"center": v(13.47, 32) * mm, "radius": 0.5 * mm});
            skCircle(sketch, "E2.14.7.0", {"center": v(13.47, 29.47) * mm, "radius": 0.5 * mm});
            skCircle(sketch, "E2.14.8.0", {"center": v(13.47, 26.93) * mm, "radius": 0.5 * mm});
            skCircle(sketch, "E2.14.9.0", {"center": v(13.47, 24.39) * mm, "radius": 0.5 * mm});
            skCircle(sketch, "E2.14.10.0", {"center": v(13.47, 21.85) * mm, "radius": 0.5 * mm});
            skCircle(sketch, "E2.14.11.0", {"center": v(13.47, 19.3) * mm, "radius": 0.5 * mm});
            skCircle(sketch, "E2.14.12.0", {"center": v(13.47, 16.77) * mm, "radius": 0.5 * mm});
            skCircle(sketch, "E2.14.13.0", {"center": v(13.47, 14.23) * mm, "radius": 0.5 * mm});
            skCircle(sketch, "E2.14.14.0", {"center": v(13.47, 11.69) * mm, "radius": 0.5 * mm});
            skCircle(sketch, "E2.14.15.0", {"center": v(13.47, 9.15) * mm, "radius": 0.5 * mm});
            skCircle(sketch, "E2.14.16.0", {"center": v(13.47, 6.6) * mm, "radius": 0.5 * mm});
            skCircle(sketch, "E2.14.17.0", {"center": v(13.47, 4.07) * mm, "radius": 0.5 * mm});
            skCircle(sketch, "E2.14.18.0", {"center": v(13.47, 1.53) * mm, "radius": 0.5 * mm});
            skCircle(sketch, "E2.14.19.0", {"center": v(13.47, -1.01) * mm, "radius": 0.5 * mm});
            skCircle(sketch, "E2.14.20.0", {"center": v(13.47, -3.55) * mm, "radius": 0.5 * mm});
            skCircle(sketch, "E2.14.21.0", {"center": v(13.47, -6.1) * mm, "radius": 0.5 * mm});
            skCircle(sketch, "E2.14.22.0", {"center": v(13.47, -8.63) * mm, "radius": 0.5 * mm});
            skCircle(sketch, "E2.14.23.0", {"center": v(13.47, -11.17) * mm, "radius": 0.5 * mm});
            skLineSegment(sketch, "E2.direction1", {"start": v(-22.1, 47.25) * mm, "end": v(-19.55, 47.25) * mm, "construction": true});
            skLineSegment(sketch, "E2.direction2", {"start": v(-22.1, 47.25) * mm, "end": v(-22.1, 44.7) * mm, "construction": true});
            skCircle(sketch, "E3.0.15.0", {"center": v(16, 47.25) * mm, "radius": 0.5 * mm});
            skCircle(sketch, "E3.0.15.1", {"center": v(16, 44.7) * mm, "radius": 0.5 * mm});
            skCircle(sketch, "E3.0.15.2", {"center": v(16, 42.17) * mm, "radius": 0.5 * mm});
            skCircle(sketch, "E3.0.15.3", {"center": v(16, 39.63) * mm, "radius": 0.5 * mm});
            skCircle(sketch, "E3.0.15.4", {"center": v(16, 37.09) * mm, "radius": 0.5 * mm});
            skCircle(sketch, "E3.0.15.5", {"center": v(16, 34.55) * mm, "radius": 0.5 * mm});
            skCircle(sketch, "E3.0.15.6", {"center": v(16, 32) * mm, "radius": 0.5 * mm});
            skCircle(sketch, "E3.0.15.7", {"center": v(16, 29.47) * mm, "radius": 0.5 * mm});
            skCircle(sketch, "E3.0.15.8", {"center": v(16, 26.93) * mm, "radius": 0.5 * mm});
            skCircle(sketch, "E3.0.15.9", {"center": v(16, 24.39) * mm, "radius": 0.5 * mm});
            skCircle(sketch, "E3.0.15.10", {"center": v(16, 21.85) * mm, "radius": 0.5 * mm});
            skCircle(sketch, "E3.0.15.11", {"center": v(16, 19.3) * mm, "radius": 0.5 * mm});
            skCircle(sketch, "E3.0.15.12", {"center": v(16, 16.77) * mm, "radius": 0.5 * mm});
            skCircle(sketch, "E3.0.15.13", {"center": v(16, 14.23) * mm, "radius": 0.5 * mm});
            skCircle(sketch, "E3.0.15.14", {"center": v(16, 11.69) * mm, "radius": 0.5 * mm});
            skCircle(sketch, "E3.0.15.15", {"center": v(16, 9.15) * mm, "radius": 0.5 * mm});
            skCircle(sketch, "E3.0.15.16", {"center": v(16, 6.6) * mm, "radius": 0.5 * mm});
            skCircle(sketch, "E3.0.15.17", {"center": v(16, 4.07) * mm, "radius": 0.5 * mm});
            skCircle(sketch, "E3.0.15.18", {"center": v(16, 1.53) * mm, "radius": 0.5 * mm});
            skCircle(sketch, "E3.0.15.19", {"center": v(16, -1.01) * mm, "radius": 0.5 * mm});
            skCircle(sketch, "E3.0.15.20", {"center": v(16, -3.55) * mm, "radius": 0.5 * mm});
            skCircle(sketch, "E3.0.15.21", {"center": v(16, -6.1) * mm, "radius": 0.5 * mm});
            skCircle(sketch, "E3.0.15.22", {"center": v(16, -8.63) * mm, "radius": 0.5 * mm});
            skCircle(sketch, "E3.0.15.23", {"center": v(16, -11.17) * mm, "radius": 0.5 * mm});
            skCircle(sketch, "E3.0.16.0", {"center": v(18.55, 47.25) * mm, "radius": 0.5 * mm});
            skCircle(sketch, "E3.0.16.1", {"center": v(18.55, 44.7) * mm, "radius": 0.5 * mm});
            skCircle(sketch, "E3.0.16.2", {"center": v(18.55, 42.17) * mm, "radius": 0.5 * mm});
            skCircle(sketch, "E3.0.16.3", {"center": v(18.55, 39.63) * mm, "radius": 0.5 * mm});
            skCircle(sketch, "E3.0.16.4", {"center": v(18.55, 37.09) * mm, "radius": 0.5 * mm});
            skCircle(sketch, "E3.0.16.5", {"center": v(18.55, 34.55) * mm, "radius": 0.5 * mm});
            skCircle(sketch, "E3.0.16.6", {"center": v(18.55, 32) * mm, "radius": 0.5 * mm});
            skCircle(sketch, "E3.0.16.7", {"center": v(18.55, 29.47) * mm, "radius": 0.5 * mm});
            skCircle(sketch, "E3.0.16.8", {"center": v(18.55, 26.93) * mm, "radius": 0.5 * mm});
            skCircle(sketch, "E3.0.16.9", {"center": v(18.55, 24.39) * mm, "radius": 0.5 * mm});
            skCircle(sketch, "E3.0.16.10", {"center": v(18.55, 21.85) * mm, "radius": 0.5 * mm});
            skCircle(sketch, "E3.0.16.11", {"center": v(18.55, 19.3) * mm, "radius": 0.5 * mm});
            skCircle(sketch, "E3.0.16.12", {"center": v(18.55, 16.77) * mm, "radius": 0.5 * mm});
            skCircle(sketch, "E3.0.16.13", {"center": v(18.55, 14.23) * mm, "radius": 0.5 * mm});
            skCircle(sketch, "E3.0.16.14", {"center": v(18.55, 11.69) * mm, "radius": 0.5 * mm});
            skCircle(sketch, "E3.0.16.15", {"center": v(18.55, 9.15) * mm, "radius": 0.5 * mm});
            skCircle(sketch, "E3.0.16.16", {"center": v(18.55, 6.6) * mm, "radius": 0.5 * mm});
            skCircle(sketch, "E3.0.16.17", {"center": v(18.55, 4.07) * mm, "radius": 0.5 * mm});
            skCircle(sketch, "E3.0.16.18", {"center": v(18.55, 1.53) * mm, "radius": 0.5 * mm});
            skCircle(sketch, "E3.0.16.19", {"center": v(18.55, -1.01) * mm, "radius": 0.5 * mm});
            skCircle(sketch, "E3.0.16.20", {"center": v(18.55, -3.55) * mm, "radius": 0.5 * mm});
            skCircle(sketch, "E3.0.16.21", {"center": v(18.55, -6.1) * mm, "radius": 0.5 * mm});
            skCircle(sketch, "E3.0.16.22", {"center": v(18.55, -8.63) * mm, "radius": 0.5 * mm});
            skCircle(sketch, "E3.0.16.23", {"center": v(18.55, -11.17) * mm, "radius": 0.5 * mm});
            skCircle(sketch, "E3.0.17.0", {"center": v(21.09, 47.25) * mm, "radius": 0.5 * mm});
            skCircle(sketch, "E3.0.17.1", {"center": v(21.09, 44.7) * mm, "radius": 0.5 * mm});
            skCircle(sketch, "E3.0.17.2", {"center": v(21.09, 42.17) * mm, "radius": 0.5 * mm});
            skCircle(sketch, "E3.0.17.3", {"center": v(21.09, 39.63) * mm, "radius": 0.5 * mm});
            skCircle(sketch, "E3.0.17.4", {"center": v(21.09, 37.09) * mm, "radius": 0.5 * mm});
            skCircle(sketch, "E3.0.17.5", {"center": v(21.09, 34.55) * mm, "radius": 0.5 * mm});
            skCircle(sketch, "E3.0.17.6", {"center": v(21.09, 32) * mm, "radius": 0.5 * mm});
            skCircle(sketch, "E3.0.17.7", {"center": v(21.09, 29.47) * mm, "radius": 0.5 * mm});
            skCircle(sketch, "E3.0.17.8", {"center": v(21.09, 26.93) * mm, "radius": 0.5 * mm});
            skCircle(sketch, "E3.0.17.9", {"center": v(21.09, 24.39) * mm, "radius": 0.5 * mm});
            skCircle(sketch, "E3.0.17.10", {"center": v(21.09, 21.85) * mm, "radius": 0.5 * mm});
            skCircle(sketch, "E3.0.17.11", {"center": v(21.09, 19.3) * mm, "radius": 0.5 * mm});
            skCircle(sketch, "E3.0.17.12", {"center": v(21.09, 16.77) * mm, "radius": 0.5 * mm});
            skCircle(sketch, "E3.0.17.13", {"center": v(21.09, 14.23) * mm, "radius": 0.5 * mm});
            skCircle(sketch, "E3.0.17.14", {"center": v(21.09, 11.69) * mm, "radius": 0.5 * mm});
            skCircle(sketch, "E3.0.17.15", {"center": v(21.09, 9.15) * mm, "radius": 0.5 * mm});
            skCircle(sketch, "E3.0.17.16", {"center": v(21.09, 6.6) * mm, "radius": 0.5 * mm});
            skCircle(sketch, "E3.0.17.17", {"center": v(21.09, 4.07) * mm, "radius": 0.5 * mm});
            skCircle(sketch, "E3.0.17.18", {"center": v(21.09, 1.53) * mm, "radius": 0.5 * mm});
            skCircle(sketch, "E3.0.17.19", {"center": v(21.09, -1.01) * mm, "radius": 0.5 * mm});
            skCircle(sketch, "E3.0.17.20", {"center": v(21.09, -3.55) * mm, "radius": 0.5 * mm});
            skCircle(sketch, "E3.0.17.21", {"center": v(21.09, -6.1) * mm, "radius": 0.5 * mm});
            skCircle(sketch, "E3.0.17.22", {"center": v(21.09, -8.63) * mm, "radius": 0.5 * mm});
            skCircle(sketch, "E3.0.17.23", {"center": v(21.09, -11.17) * mm, "radius": 0.5 * mm});
            skCircle(sketch, "E4", {"center": v(-14.47, 42.17) * mm, "radius": 1.5 * mm});
            skCircle(sketch, "E5", {"center": v(-14.47, -3.55) * mm, "radius": 1.5 * mm});
            skCircle(sketch, "E6", {"center": v(18.55, 11.69) * mm, "radius": 1.5 * mm});
            skSolve(sketch);
        }
        {
            var Q0;
            Q0=makeQuery(id+"F0.imprint","IMPRINT",FACE,{"disambiguationData":[TD([[makeQuery(id+"F0.imprint","IMPRINT",EDGE,{"derivedFrom":sQuery(id+"F0.wireOp",EDGE,"E0.bottom")}),-1.0]])]});
            extrude(context, id + "F1", {"entities" : qUnion([Q0]), "depth" : 1.6 * mm, "offsetDistance" : 25 * mm});
        }
        {
            var Q0;
            Q0=makeQuery(id+"F1.opExtrude","CAP_FACE",FACE,{"disambiguationData":[OSD([sQuery(id+"F0.wireOp",EDGE,"E0.bottom"),sQuery(id+"F0.wireOp",EDGE,"E0.top"),sQuery(id+"F0.wireOp",EDGE,"E0.left"),sQuery(id+"F0.wireOp",EDGE,"E0.right"),sQuery(id+"F0.wireOp",EDGE,"6mtzxuK8-kbeM-4C7B-xpll-Af9zMKx6uoet"),sQuery(id+"F0.wireOp",EDGE,"zsmSpqsC-8B0L-KlKL-wEcU-SULrlTbzQN1M"),sQuery(id+"F0.wireOp",EDGE,"DMHRSxKd-PC2k-h0UT-FV1q-sQdZEGIy2eZX"),sQuery(id+"F0.wireOp",EDGE,"j1i3zPgz-FiHg-5LTF-wwvy-UbnwsyVD2wbp")])],"isStart":false});
            var sketch = newSketch(context, id + "F2", { "sketchPlane" : qUnion([Q0])});
            skLineSegment(sketch, "E7.bottom", {"start": v(-19.1, -17.17) * mm, "end": v(-7.1, -17.17) * mm});
            skLineSegment(sketch, "E7.top", {"start": v(-19.1, -33.17) * mm, "end": v(-7.1, -33.17) * mm});
            skLineSegment(sketch, "E7.left", {"start": v(-19.1, -17.17) * mm, "end": v(-19.1, -33.17) * mm});
            skLineSegment(sketch, "E7.right", {"start": v(-7.1, -17.17) * mm, "end": v(-7.1, -33.17) * mm});
            skSolve(sketch);
        }
        {
            var Q0;
            {var subQ0=sQuery(id+"F2.wireOp",EDGE,"E7.bottom");Q0=makeQuery(id+"F2.imprint","IMPRINT",FACE,{"disambiguationData":[TD([[makeQuery(id+"F2.imprint","IMPRINT",EDGE,{"derivedFrom":subQ0}),-1.0]])]});}
            var Q1;
            {var subQ0=sQuery(id+"F2.wireOp",EDGE,"E7.top");Q1=makeQuery(id+"F2.imprint","IMPRINT",FACE,{"disambiguationData":[TD([[makeQuery(id+"F2.imprint","IMPRINT",EDGE,{"derivedFrom":subQ0}),1.0]])]});}
            var Q2;
            {var subQ0=sQuery(id+"F2.wireOp",EDGE,"E7.left");var subQ1=makeQuery(id+"F1.opExtrude","CAP_EDGE",EDGE,{"disambiguationData":[OSD([sQuery(id+"F0.wireOp",EDGE,"E2.1.22.0")])],"isStart":false});var subQ2=makeQuery(id+"F2.imprint","INTERSECT",VERTEX,{"disambiguationData":[OD(0.0)],"derivedFrom":[subQ1,subQ0]});Q2=makeQuery(id+"F2.imprint","IMPRINT",FACE,{"disambiguationData":[TD([[makeQuery(id+"F2.imprint","IMPRINT",EDGE,{"disambiguationData":[TD([[subQ2,-1.0]])],"derivedFrom":subQ0}),1.0]])]});}
            var Q3;
            {var subQ0=sQuery(id+"F2.wireOp",EDGE,"E7.left");var subQ1=sQuery(id+"F2.wireOp",EDGE,"E7.bottom");var subQ2=makeQuery(id+"F2.imprint","INTERSECT",VERTEX,{"derivedFrom":[subQ1,subQ0]});Q3=makeQuery(id+"F2.imprint","IMPRINT",FACE,{"disambiguationData":[TD([[makeQuery(id+"F2.imprint","IMPRINT",EDGE,{"disambiguationData":[TD([[subQ2,-1.0]])],"derivedFrom":subQ1}),-1.0]])]});}
            var Q4;
            {var subQ0=sQuery(id+"F2.wireOp",EDGE,"E7.bottom");var subQ1=makeQuery(id+"F1.opExtrude","CAP_EDGE",EDGE,{"disambiguationData":[OSD([sQuery(id+"F0.wireOp",EDGE,"E2.2.21.0")])],"isStart":false});var subQ2=makeQuery(id+"F2.imprint","INTERSECT",VERTEX,{"disambiguationData":[OD(0.0)],"derivedFrom":[subQ1,subQ0]});Q4=makeQuery(id+"F2.imprint","IMPRINT",FACE,{"disambiguationData":[TD([[makeQuery(id+"F2.imprint","IMPRINT",EDGE,{"disambiguationData":[TD([[subQ2,-1.0]])],"derivedFrom":subQ0}),-1.0]])]});}
            var Q5;
            {var subQ0=sQuery(id+"F2.wireOp",EDGE,"E7.left");var subQ1=makeQuery(id+"F1.opExtrude","CAP_EDGE",EDGE,{"disambiguationData":[OSD([sQuery(id+"F0.wireOp",EDGE,"E2.1.23.0")])],"isStart":false});var subQ2=makeQuery(id+"F2.imprint","INTERSECT",VERTEX,{"disambiguationData":[OD(0.0)],"derivedFrom":[subQ1,subQ0]});Q5=makeQuery(id+"F2.imprint","IMPRINT",FACE,{"disambiguationData":[TD([[makeQuery(id+"F2.imprint","IMPRINT",EDGE,{"disambiguationData":[TD([[subQ2,-1.0]])],"derivedFrom":subQ0}),1.0]])]});}
            var Q6;
            {var subQ0=sQuery(id+"F2.wireOp",EDGE,"E7.bottom");var subQ1=makeQuery(id+"F1.opExtrude","CAP_EDGE",EDGE,{"disambiguationData":[OSD([sQuery(id+"F0.wireOp",EDGE,"E2.3.21.0")])],"isStart":false});var subQ2=makeQuery(id+"F2.imprint","INTERSECT",VERTEX,{"disambiguationData":[OD(0.0)],"derivedFrom":[subQ1,subQ0]});Q6=makeQuery(id+"F2.imprint","IMPRINT",FACE,{"disambiguationData":[TD([[makeQuery(id+"F2.imprint","IMPRINT",EDGE,{"disambiguationData":[TD([[subQ2,-1.0]])],"derivedFrom":subQ0}),-1.0]])]});}
            var Q7;
            {var subQ0=sQuery(id+"F2.wireOp",EDGE,"E7.bottom");var subQ1=makeQuery(id+"F1.opExtrude","CAP_EDGE",EDGE,{"disambiguationData":[OSD([sQuery(id+"F0.wireOp",EDGE,"E2.4.21.0")])],"isStart":false});var subQ2=makeQuery(id+"F2.imprint","INTERSECT",VERTEX,{"disambiguationData":[OD(0.0)],"derivedFrom":[subQ1,subQ0]});Q7=makeQuery(id+"F2.imprint","IMPRINT",FACE,{"disambiguationData":[TD([[makeQuery(id+"F2.imprint","IMPRINT",EDGE,{"disambiguationData":[TD([[subQ2,-1.0]])],"derivedFrom":subQ0}),-1.0]])]});}
            var Q8;
            {var subQ0=sQuery(id+"F2.wireOp",EDGE,"E7.bottom");var subQ1=makeQuery(id+"F1.opExtrude","CAP_EDGE",EDGE,{"disambiguationData":[OSD([sQuery(id+"F0.wireOp",EDGE,"E2.5.21.0")])],"isStart":false});var subQ2=makeQuery(id+"F2.imprint","INTERSECT",VERTEX,{"disambiguationData":[OD(0.0)],"derivedFrom":[subQ1,subQ0]});Q8=makeQuery(id+"F2.imprint","IMPRINT",FACE,{"disambiguationData":[TD([[makeQuery(id+"F2.imprint","IMPRINT",EDGE,{"disambiguationData":[TD([[subQ2,-1.0]])],"derivedFrom":subQ0}),-1.0]])]});}
            extrude(context, id + "F3", {"entities" : qUnion([Q0, Q1, Q2, Q3, Q4, Q5, Q6, Q7, Q8]), "depth" : 11 * mm, "offsetDistance" : 25 * mm});
        }
        {
            var Q0;
            Q0=makeQuery(id+"F1.opExtrude","SWEPT_EDGE",EDGE,{"disambiguationData":[OSD([sQuery(id+"F0.wireOp",EDGE,"E0.top"),sQuery(id+"F0.wireOp",EDGE,"E0.left")])]});
            var Q1;
            Q1=makeQuery(id+"F1.opExtrude","SWEPT_EDGE",EDGE,{"disambiguationData":[OSD([sQuery(id+"F0.wireOp",EDGE,"E0.bottom"),sQuery(id+"F0.wireOp",EDGE,"E0.left")])]});
            var Q2;
            Q2=makeQuery(id+"F1.opExtrude","SWEPT_EDGE",EDGE,{"disambiguationData":[OSD([sQuery(id+"F0.wireOp",EDGE,"E0.bottom"),sQuery(id+"F0.wireOp",EDGE,"E0.right")])]});
            var Q3;
            Q3=makeQuery(id+"F1.opExtrude","SWEPT_EDGE",EDGE,{"disambiguationData":[OSD([sQuery(id+"F0.wireOp",EDGE,"E0.top"),sQuery(id+"F0.wireOp",EDGE,"E0.right")])]});
            fillet(context, id + "F4", {"entities" : qUnion([Q0, Q1, Q2, Q3]), "radius" : 2 * mm, "tangentPropagation" : true, "allowEdgeOverflow" : false});
        }
    });
